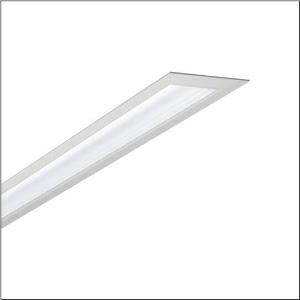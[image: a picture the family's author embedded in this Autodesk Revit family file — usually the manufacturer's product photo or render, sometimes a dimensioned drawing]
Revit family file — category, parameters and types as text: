
# Revit family: silica_r_5mx11bd1w4a_3352
name_source: partatom
category: Lighting Fixtures
units: mm (PartAtom-declared; Revit-internal decimal feet)

## family parameters
Cut with Voids When Loaded = No
Host = Face
Light Source = No
Part Type = Normal
Room Calculation Point = No
Round Connector Dimension = Use Diameter
Shared = No

## types (1)
- --- (1 x LED, 4950 lm, 29.3 W, 4000K)
    Apparent Load = 29 VA
    CIE Flux Codes = 82 97 100 100 100
    Color Rendering = 80
    Color Temperature = 4000K
    Default Elevation = 1800 mm
    Description = Silica®, office luminaire, of aluminium, light emission: direct distribution, primary light characteristic: symmetric, installation type: recessed, LED, rated luminous flux: 4.950lm, luminous efficacy: 169lm/W, light colour: 840, colour temperature: 4000K, control gear: ECG DALI, with terminal, 3+2-pole, max. 2.5mm², mains connection: 230V, AC, 50/60Hz, rated input power: 29W, luminaire housing, of aluminium, matt pure white (RAL 9010), length: 1.462mm, width: 93mm, height: 60mm, end cap, of diecast zinc, pure white (RAL 9010), protection rating (complete): IP20, insulation class (complete): insulation class I (protective earthing), certification: CE, permissible operating ambient temperature: 0..+35°C, standard: EN 50419, packaging unit: 1 piece
    Height = 0 mm  [stored 0 ft]
    Lamp = 1 x LED
    Lamp Light Flux = 4950 lm
    Lamp Power = 29.3 W
    Lamp count = 1
    Length = 1462 mm
    Luminous efficacy = 169 lm/W
    Manufacturer = Siteco
    ModVariant = No
    Model = 5MX11BD1W4A
    Mounting Place = Ceiling
    Mounting Type = Recessed
    Number of Poles = 1
    OnlyDefault = Yes
    Power Factor = 1
    Product Name = Silica®
    Product group = office luminaire | ceiling recessed
    ProductGroupID = 401
    Protection Class = Protection class I
    Protection Degree = IP 20
    RLX_Detail_Level = 1
    RLX_Emergency_Light_Flux = 0 lm
    RLX_Emergency_Type = 0
    RLX_Emergency_Type_DB = No
    RlxData = <blob elided: 24033 chars, md5=11b78be9>
    Socket = socket
    Standby Power = 0 W
    System Light Flux = 4950 lm
    System Power = 29 W
    Type Comments = factory setting: luminous flux: 100 % | dim-lin: 254 | 163 mA
    Type Image = l_1004825.jpg
    URL = http://relux.com
    VarID = @adj_155382
    Voltage = 0 V
    Weight = 0.00 kg
    Width = 93 mm

note: [stored X ft] marks values corroborated as IEEE doubles in the binary element streams (Revit-internal decimal feet)

## geometry (parser evidence)
native form markers: Blend x4, Sweep x11
no freeform markers — native parametric forms only
